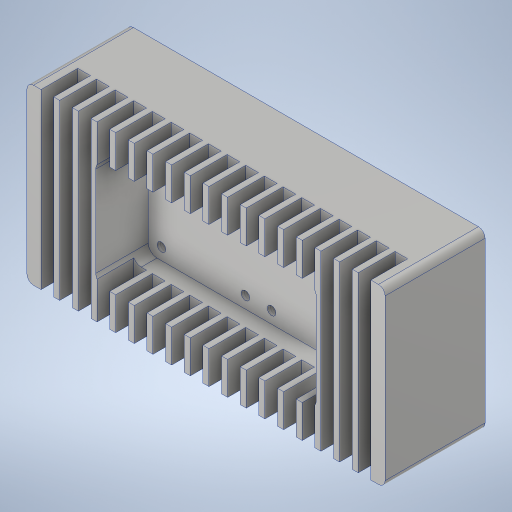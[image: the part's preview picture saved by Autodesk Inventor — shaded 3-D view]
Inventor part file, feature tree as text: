
AUTODESK INVENTOR PART (.ipt)
format: ipt  version: 2023.4 (Build 274418000, 418)  size: 451,072 bytes
history: native  units: in
note: dims shown in document units (in); Inventor stores cm internally (conversion verified against a paired STEP export)
features: sketch x5, extrude x4, fillet x2, pattern_linear x1, hole x1, projected_geometry x1
ambient origin geometry x8: Origin, YZ Plane, XZ Plane, XY Plane, X Axis, Y Axis, Z Axis, Center Point
bodies: Solid1 (feature_tree)
feature tree (14):
  extrude  "Extrusion1"  Depth=2.6in
  extrude  "Extrusion2"  Depth=3.3071in
  fillet  "Fillet1"  Radius=1.6142in
  sketch  "Sketch4"  dims[d6=0.7874in d7=0.0in d8=0.13in]
  sketch  "Sketch5"  dims[d20=0.212in]
  extrude  "Extrusion3"  Depth=0.13in
  pattern_linear  "Rectangular Pattern1"  Spacing1=0.5512in  [1 undecoded]
  fillet  "Fillet2"  Radius=0.28in
  extrude  "Extrusion4"  Depth=0.1in
  hole  "Hole2"  [1 undecoded]
  sketch  "Sketch1"  dims[d0=5.375in d1=2.6in]
  sketch  "Sketch2"  dims[d2=1.5in d3=0.0in d4=3.3071in d5=1.6142in]
  projected_geometry  "Projected Loop1"
  sketch  "Sketch7"  dims[d21=0.19in d22=0.5512in d23=0.0in d24=7.0866in d26=0.28in d27=0.1in d29=4.675in d30=2.2in d31=2.6in d32=0.2in d33=5.375in d34=0.35in d35=0.13in d36=0.3in d37=0.0in d42=1.2598in d43=1.2598in d44=1.2598in d45=1.2598in d46=0.1969in d47=1.6142in d48=0.1772in d49=0.13in d50=0.328in d51=0.375in d52=0.25in d53=0.5635in d54=1.0in d55=0.8108in]
note: 2 required parameter values undecoded (feature->parameter linkage not recoverable at this tier; creation-order binding heuristic only, values carry confidence <= 0.55)
